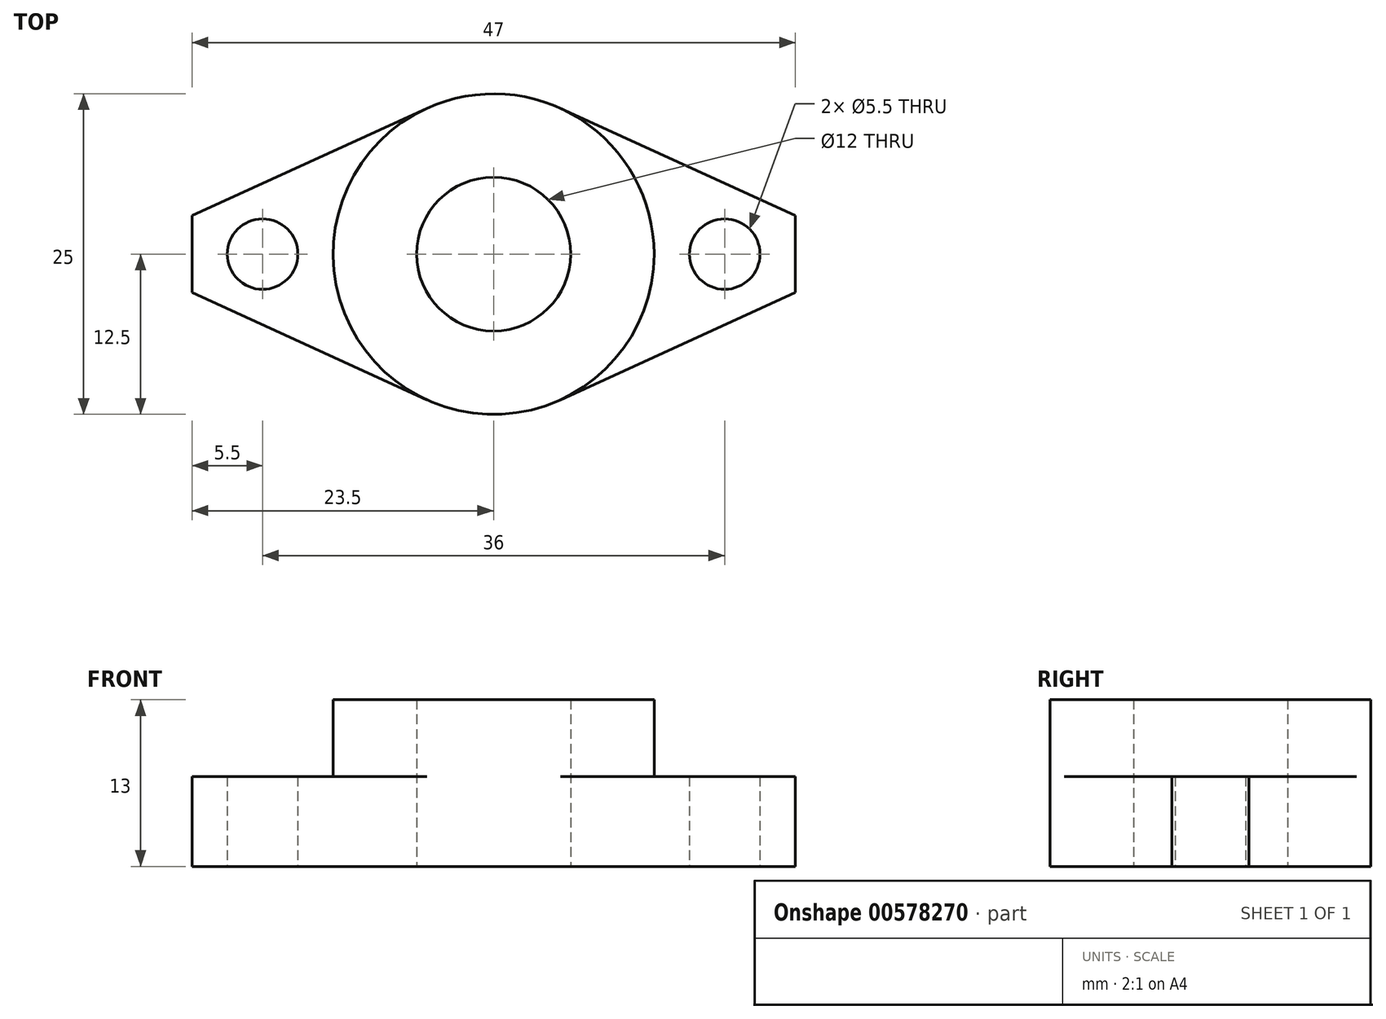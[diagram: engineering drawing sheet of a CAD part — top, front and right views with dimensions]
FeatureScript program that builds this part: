
annotation { "Feature Type Name" : "Feature", "Feature Type Description" : "" }
export const myFeature = defineFeature(function(context is Context, id is Id, definition is map)
    precondition{}
    {
        {
            var Q0;
            Q0=qCreatedBy(makeId("Top.planeOp"),FACE);
            var sketch = newSketch(context, id + "F0", { "sketchPlane" : qUnion([Q0])});
            skCircle(sketch, "E0", {"center": v(0, 0) * mm, "radius": 12.5 * mm});
            skCircle(sketch, "E1", {"center": v(0, 0) * mm, "radius": 6 * mm});
            skCircle(sketch, "E2", {"center": v(18, 0) * mm, "radius": 2.75 * mm});
            skCircle(sketch, "E3", {"center": v(-18, 0) * mm, "radius": 2.75 * mm});
            skLineSegment(sketch, "E4", {"start": v(-5.2, 11.37) * mm, "end": v(-23.5, 3) * mm});
            skLineSegment(sketch, "E5.MirrorCS", {"start": v(-5.2, -11.37) * mm, "end": v(-23.5, -3) * mm});
            skLineSegment(sketch, "E6", {"start": v(-23.5, 3) * mm, "end": v(-23.5, -3) * mm});
            skLineSegment(sketch, "E7.MirrorCS", {"start": v(5.2, 11.37) * mm, "end": v(23.5, 3) * mm});
            skLineSegment(sketch, "E8.MirrorCS", {"start": v(23.5, 3) * mm, "end": v(23.5, -3) * mm});
            skLineSegment(sketch, "E9.MirrorCS", {"start": v(5.2, -11.37) * mm, "end": v(23.5, -3) * mm});
            skLineSegment(sketch, "E10", {"start": v(-23.5, 0) * mm, "end": v(23.5, 0) * mm});
            skSolve(sketch);
        }
        {
            var Q0;
            Q0=makeQuery(id+"F0.imprint","IMPRINT",FACE,{"disambiguationData":[TD([[makeQuery(id+"F0.imprint","IMPRINT",EDGE,{"derivedFrom":sQuery(id+"F0.wireOp",EDGE,"E1")}),-1.0]])]});
            extrude(context, id + "F1", {"entities" : qUnion([Q0]), "depth" : 13 * mm, "offsetDistance" : 25 * mm});
        }
        {
            var Q0;
            Q0=makeQuery(id+"F0.imprint","IMPRINT",FACE,{"disambiguationData":[TD([[makeQuery(id+"F0.imprint","IMPRINT",EDGE,{"derivedFrom":sQuery(id+"F0.wireOp",EDGE,"E3")}),-1.0]])]});
            var Q1;
            Q1=makeQuery(id+"F0.imprint","IMPRINT",FACE,{"disambiguationData":[TD([[makeQuery(id+"F0.imprint","IMPRINT",EDGE,{"derivedFrom":sQuery(id+"F0.wireOp",EDGE,"E2")}),-1.0]])]});
            extrude(context, id + "F2", {"entities" : qUnion([Q0, Q1]), "operationType" : NewBodyOperationType.ADD, "depth" : 7 * mm, "offsetDistance" : 25 * mm});
        }
    });
